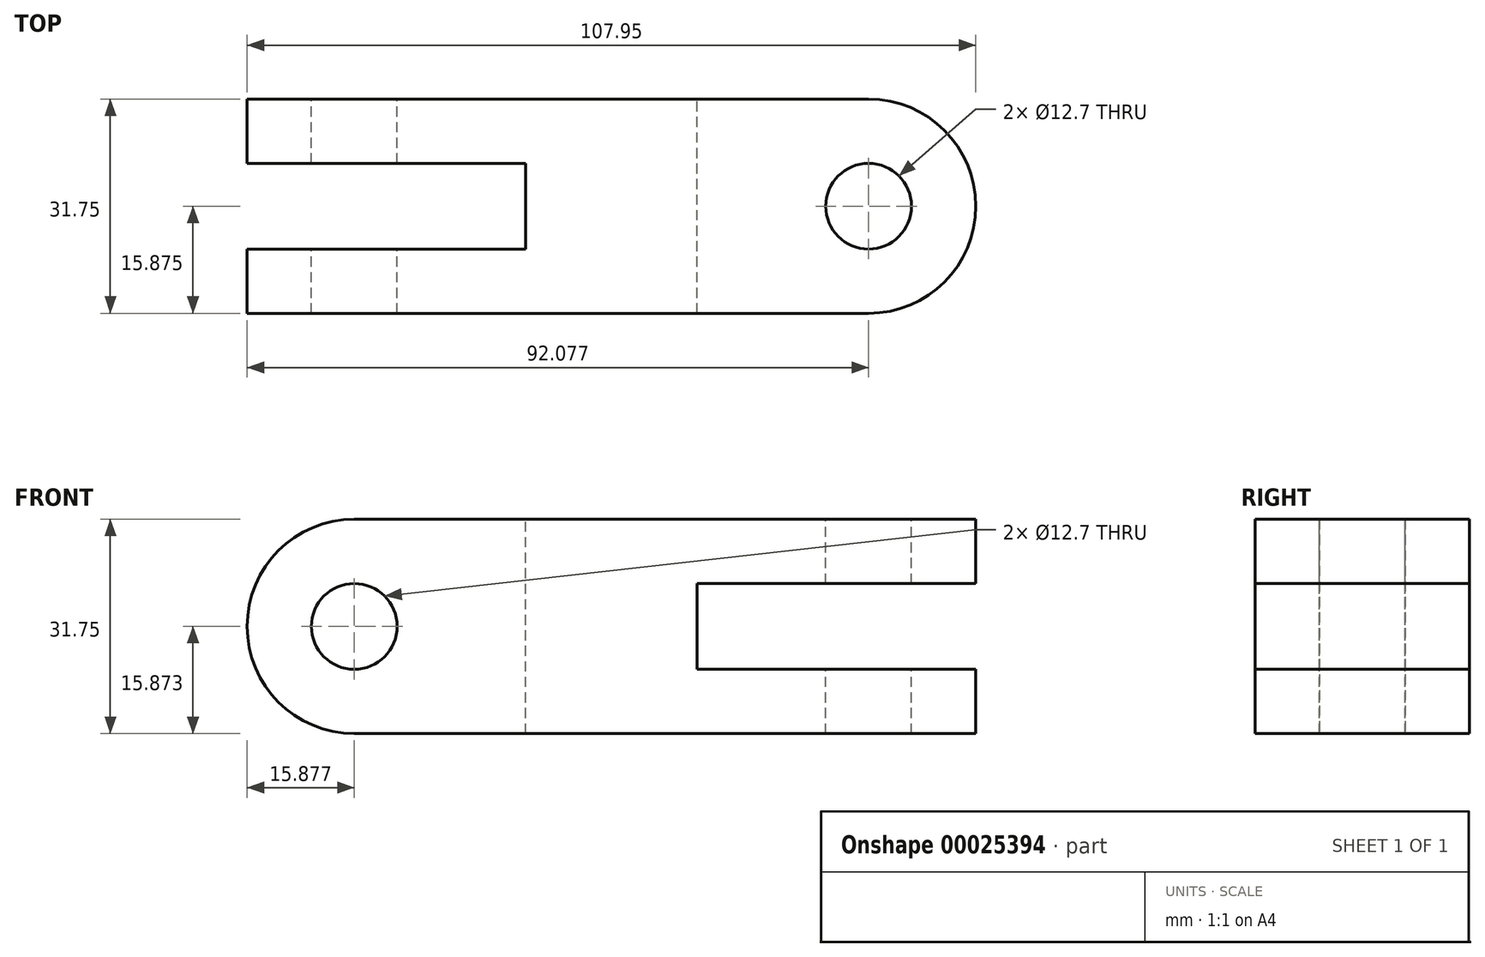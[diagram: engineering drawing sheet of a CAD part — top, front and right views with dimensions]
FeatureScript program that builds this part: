
annotation { "Feature Type Name" : "Feature", "Feature Type Description" : "" }
export const myFeature = defineFeature(function(context is Context, id is Id, definition is map)
    precondition{}
    {
        {
            var Q0;
            Q0=qCreatedBy(makeId("Front.planeOp"),FACE);
            var sketch = newSketch(context, id + "F0", { "sketchPlane" : qUnion([Q0])});
            skLineSegment(sketch, "E0.bottom", {"start": v(-46.34, 22.34) * mm, "end": v(61.61, 22.34) * mm});
            skLineSegment(sketch, "E0.top", {"start": v(-46.34, -9.41) * mm, "end": v(61.61, -9.41) * mm});
            skLineSegment(sketch, "E0.left", {"start": v(-46.34, 22.34) * mm, "end": v(-46.34, -9.41) * mm});
            skLineSegment(sketch, "E0.right", {"start": v(61.61, 22.34) * mm, "end": v(61.61, -9.41) * mm});
            skLineSegment(sketch, "E1.0", {"start": v(20.34, 12.81) * mm, "end": v(20.34, 0.11) * mm});
            skArc(sketch, "E2", {"start": v(-30.46, 22.34) * mm, "mid": v(-46.34, 6.46) * mm, "end": v(-30.46, -9.41) * mm});
            skCircle(sketch, "E3", {"center": v(-30.46, 6.46) * mm, "radius": 6.35 * mm});
            skLineSegment(sketch, "E4.trimOffspring", {"start": v(20.34, 12.81) * mm, "end": v(61.61, 12.81) * mm});
            skLineSegment(sketch, "E5.trimOffspring", {"start": v(20.34, 0.11) * mm, "end": v(61.61, 0.11) * mm});
            skSolve(sketch);
        }
        {
            var Q0;
            Q0=makeQuery(id+"F0.imprint","IMPRINT",FACE,{"disambiguationData":[TD([[makeQuery(id+"F0.imprint","IMPRINT",EDGE,{"derivedFrom":sQuery(id+"F0.wireOp",EDGE,"E1.0")}),-1.0]])]});
            extrude(context, id + "F1", {"entities" : qUnion([Q0]), "depth" : 31.75 * mm});
        }
        {
            var Q0;
            Q0=makeQuery(id+"F1.opExtrude","SWEPT_FACE",FACE,{"disambiguationData":[OSD([sQuery(id+"F0.wireOp",EDGE,"E0.bottom")])]});
            var sketch = newSketch(context, id + "F2", { "sketchPlane" : qUnion([Q0])});
            skLineSegment(sketch, "E6.0", {"start": v(-46.34, -31.75) * mm, "end": v(-46.34, 0) * mm});
            skLineSegment(sketch, "E7", {"start": v(-46.34, 0) * mm, "end": v(61.61, 0) * mm});
            skLineSegment(sketch, "E8", {"start": v(-46.34, -31.75) * mm, "end": v(61.61, -31.75) * mm});
            skLineSegment(sketch, "E9", {"start": v(61.61, -31.75) * mm, "end": v(61.61, 0) * mm});
            skLineSegment(sketch, "E10.0", {"start": v(-46.34, -9.53) * mm, "end": v(-5.06, -9.53) * mm});
            skLineSegment(sketch, "E11.0", {"start": v(-46.34, -22.23) * mm, "end": v(-5.06, -22.23) * mm});
            skLineSegment(sketch, "E12.0", {"start": v(-5.06, -22.23) * mm, "end": v(-5.06, -9.52) * mm});
            skArc(sketch, "E13", {"start": v(45.74, -31.75) * mm, "mid": v(61.61, -15.88) * mm, "end": v(45.74, 0) * mm});
            skCircle(sketch, "E14", {"center": v(45.74, -15.88) * mm, "radius": 6.35 * mm});
            skSolve(sketch);
        }
        {
            var Q0;
            {var subQ3=sQuery(id+"F2.wireOp",EDGE,"E10.0");var subQ5=sQuery(id+"F2.wireOp",EDGE,"E6.0");var subQ7=makeQuery(id+"F2.imprint","INTERSECT",VERTEX,{"derivedFrom":[subQ5,subQ3]});Q0=makeQuery(id+"F2.imprint","IMPRINT",FACE,{"disambiguationData":[TD([[makeQuery(id+"F2.imprint","IMPRINT",EDGE,{"disambiguationData":[TD([[subQ7,1.0]])],"derivedFrom":subQ5}),-1.0]])]});}
            var Q1;
            {var subQ5=sQuery(id+"F2.wireOp",EDGE,"E12.0");Q1=makeQuery(id+"F2.imprint","IMPRINT",FACE,{"disambiguationData":[TD([[makeQuery(id+"F2.imprint","IMPRINT",EDGE,{"derivedFrom":subQ5}),1.0]])]});}
            var Q2;
            Q2=makeQuery(id+"F2.imprint","IMPRINT",FACE,{"disambiguationData":[TD([[makeQuery(id+"F2.imprint","IMPRINT",EDGE,{"derivedFrom":sQuery(id+"F2.wireOp",EDGE,"E14")}),1.0]])]});
            var Q3;
            {var subQ1=sQuery(id+"F2.wireOp",EDGE,"E9");var subQ3=sQuery(id+"F2.wireOp",EDGE,"E7");var subQ5=makeQuery(id+"F2.imprint","INTERSECT",VERTEX,{"derivedFrom":[subQ3,subQ1]});Q3=makeQuery(id+"F2.imprint","IMPRINT",FACE,{"disambiguationData":[TD([[makeQuery(id+"F2.imprint","IMPRINT",EDGE,{"disambiguationData":[TD([[subQ5,1.0]])],"derivedFrom":subQ3}),-1.0]])]});}
            var Q4;
            {var subQ1=sQuery(id+"F2.wireOp",EDGE,"E9");var subQ3=sQuery(id+"F2.wireOp",EDGE,"E8");var subQ5=makeQuery(id+"F2.imprint","INTERSECT",VERTEX,{"derivedFrom":[subQ3,subQ1]});Q4=makeQuery(id+"F2.imprint","IMPRINT",FACE,{"disambiguationData":[TD([[makeQuery(id+"F2.imprint","IMPRINT",EDGE,{"disambiguationData":[TD([[subQ5,1.0]])],"derivedFrom":subQ3}),1.0]])]});}
            extrude(context, id + "F3", {"entities" : qUnion([Q0, Q1, Q2, Q3, Q4]), "operationType" : NewBodyOperationType.REMOVE, "endBound" : BoundingType.THROUGH_ALL, "oppositeDirection" : true, "depth" : 25.4 * mm});
        }
    });
